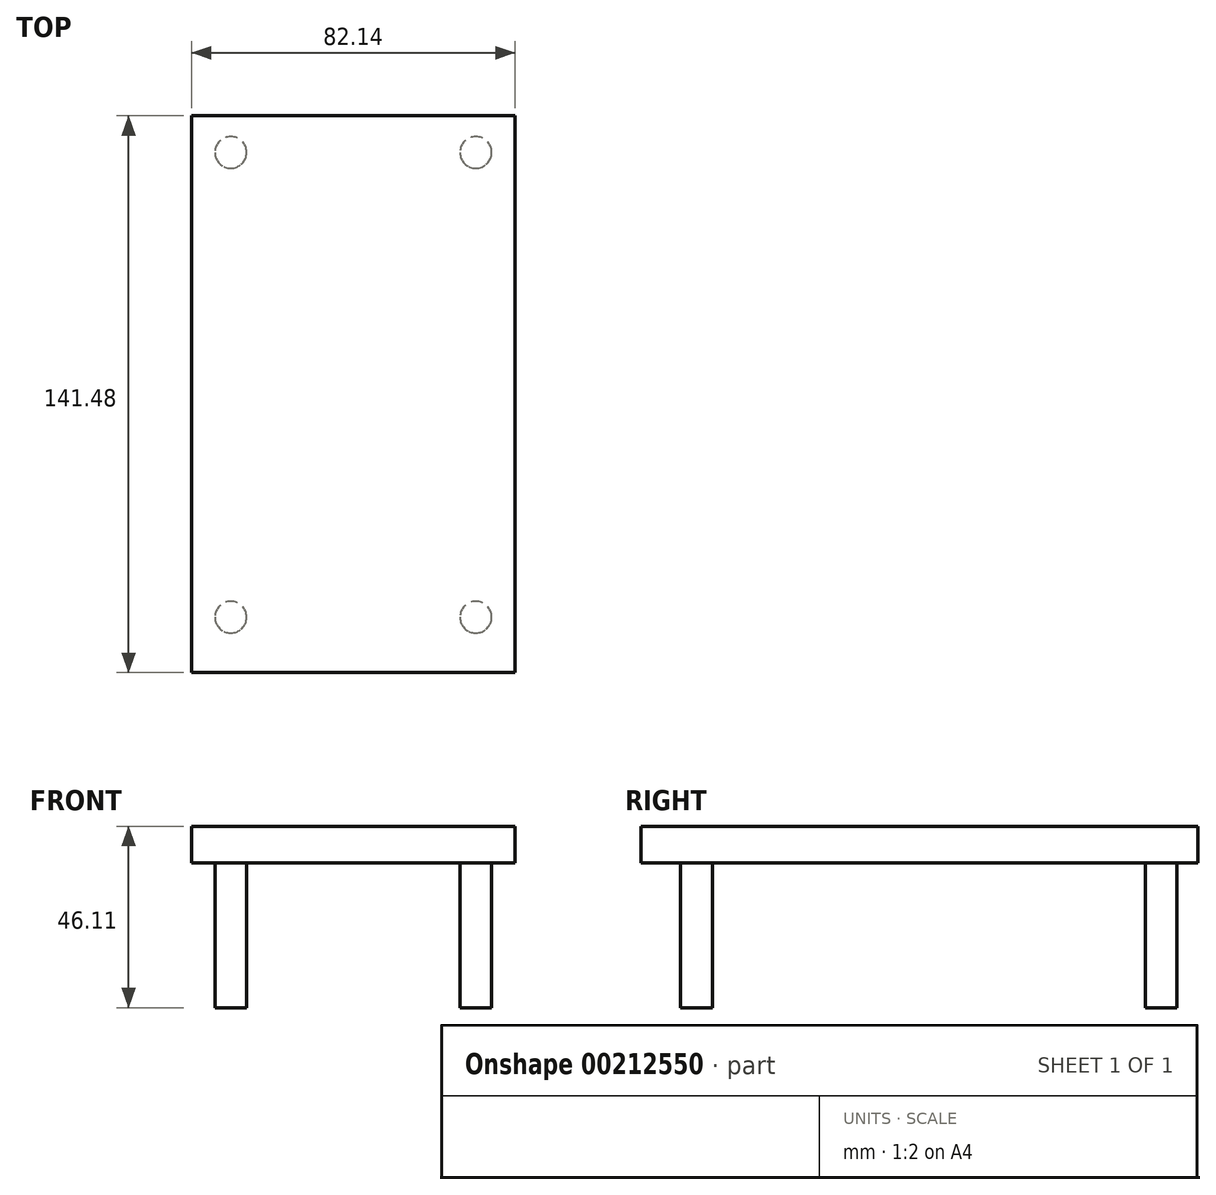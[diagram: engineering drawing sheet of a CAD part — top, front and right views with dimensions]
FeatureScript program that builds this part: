
annotation { "Feature Type Name" : "Feature", "Feature Type Description" : "" }
export const myFeature = defineFeature(function(context is Context, id is Id, definition is map)
    precondition{}
    {
        {
            var Q0;
            Q0=qCreatedBy(makeId("Front.planeOp"),FACE);
            var sketch = newSketch(context, id + "F0", { "sketchPlane" : qUnion([Q0])});
            skLineSegment(sketch, "E0.bottom", {"start": v(-41.07, 46.1) * mm, "end": v(41.07, 46.1) * mm});
            skLineSegment(sketch, "E0.top", {"start": v(-41.07, 36.76) * mm, "end": v(41.07, 36.76) * mm});
            skLineSegment(sketch, "E0.left", {"start": v(-41.07, 46.1) * mm, "end": v(-41.07, 36.76) * mm});
            skLineSegment(sketch, "E0.right", {"start": v(41.07, 46.1) * mm, "end": v(41.07, 36.76) * mm});
            skSolve(sketch);
        }
        {
            var Q0;
            Q0 = qSketchRegion(id + "F0", true);
            extrude(context, id + "F1", {"entities" : qUnion([Q0]), "oppositeDirection" : true, "depth" : 68.33 * mm, "hasSecondDirection" : true, "secondDirectionOppositeDirection" : false, "secondDirectionDepth" : 73.15 * mm});
        }
        {
            var Q0;
            Q0=qCreatedBy(makeId("Top.planeOp"),FACE);
            var sketch = newSketch(context, id + "F2", { "sketchPlane" : qUnion([Q0])});
            skCircle(sketch, "E1", {"center": v(-31.13, 59.05) * mm, "radius": 4.02 * mm});
            skCircle(sketch, "E2.MirrorC", {"center": v(31.13, 59.05) * mm, "radius": 4.02 * mm});
            skCircle(sketch, "E3.MirrorC", {"center": v(-31.13, -59.05) * mm, "radius": 4.02 * mm});
            skCircle(sketch, "E4.MirrorC", {"center": v(31.13, -59.05) * mm, "radius": 4.02 * mm});
            skSolve(sketch);
        }
        {
            var Q0;
            Q0 = qSketchRegion(id + "F2", true);
            extrude(context, id + "F3", {"entities" : qUnion([Q0]), "operationType" : NewBodyOperationType.ADD, "depth" : 45.72 * mm});
        }
    });
